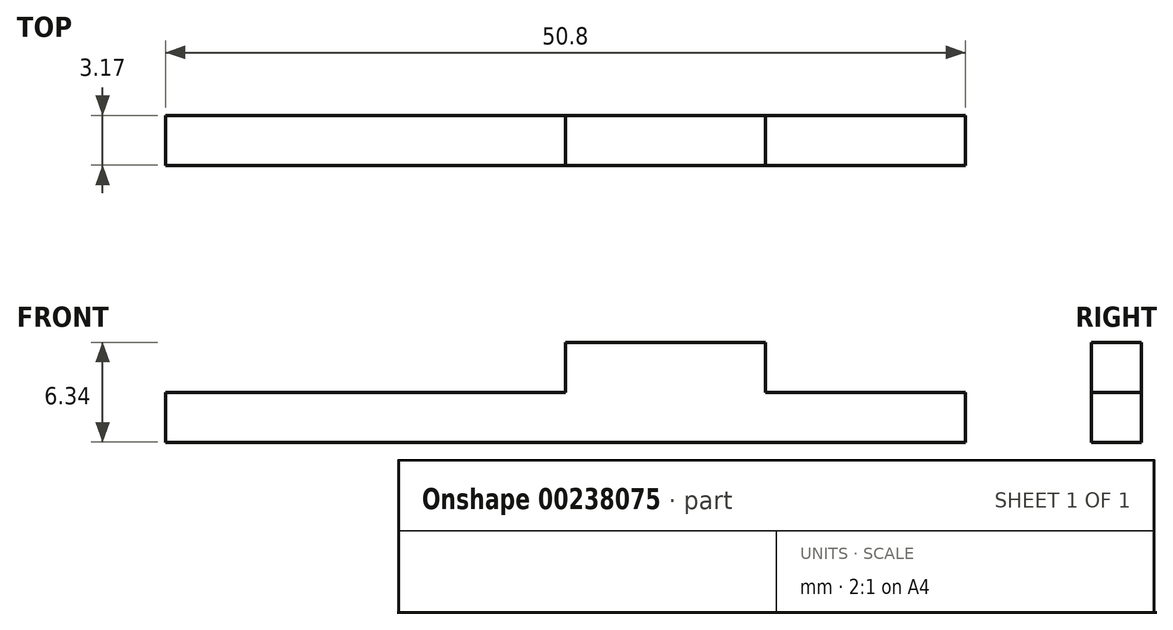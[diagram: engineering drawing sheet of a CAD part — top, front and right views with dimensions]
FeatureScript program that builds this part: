
annotation { "Feature Type Name" : "Feature", "Feature Type Description" : "" }
export const myFeature = defineFeature(function(context is Context, id is Id, definition is map)
    precondition{}
    {
        {
            var Q0;
            Q0=qCreatedBy(makeId("Front.planeOp"),FACE);
            var sketch = newSketch(context, id + "F0", { "sketchPlane" : qUnion([Q0])});
            skLineSegment(sketch, "E0.bottom", {"start": v(-25.4, 0) * mm, "end": v(25.4, 0) * mm});
            skLineSegment(sketch, "E0.top", {"start": v(-25.4, -3.17) * mm, "end": v(25.4, -3.17) * mm});
            skLineSegment(sketch, "E0.left", {"start": v(-25.4, 0) * mm, "end": v(-25.4, -3.17) * mm});
            skLineSegment(sketch, "E0.right", {"start": v(25.4, 0) * mm, "end": v(25.4, -3.17) * mm});
            skLineSegment(sketch, "E1.bottom", {"start": v(0, 3.17) * mm, "end": v(12.7, 3.17) * mm});
            skLineSegment(sketch, "E1.top", {"start": v(0, 0) * mm, "end": v(12.7, 0) * mm});
            skLineSegment(sketch, "E1.left", {"start": v(0, 3.17) * mm, "end": v(0, 0) * mm});
            skLineSegment(sketch, "E1.right", {"start": v(12.7, 3.17) * mm, "end": v(12.7, 0) * mm});
            skSolve(sketch);
        }
        {
            var Q0;
            Q0 = qSketchRegion(id + "F0", true);
            extrude(context, id + "F1", {"entities" : qUnion([Q0]), "depth" : 3.17 * mm});
        }
    });
